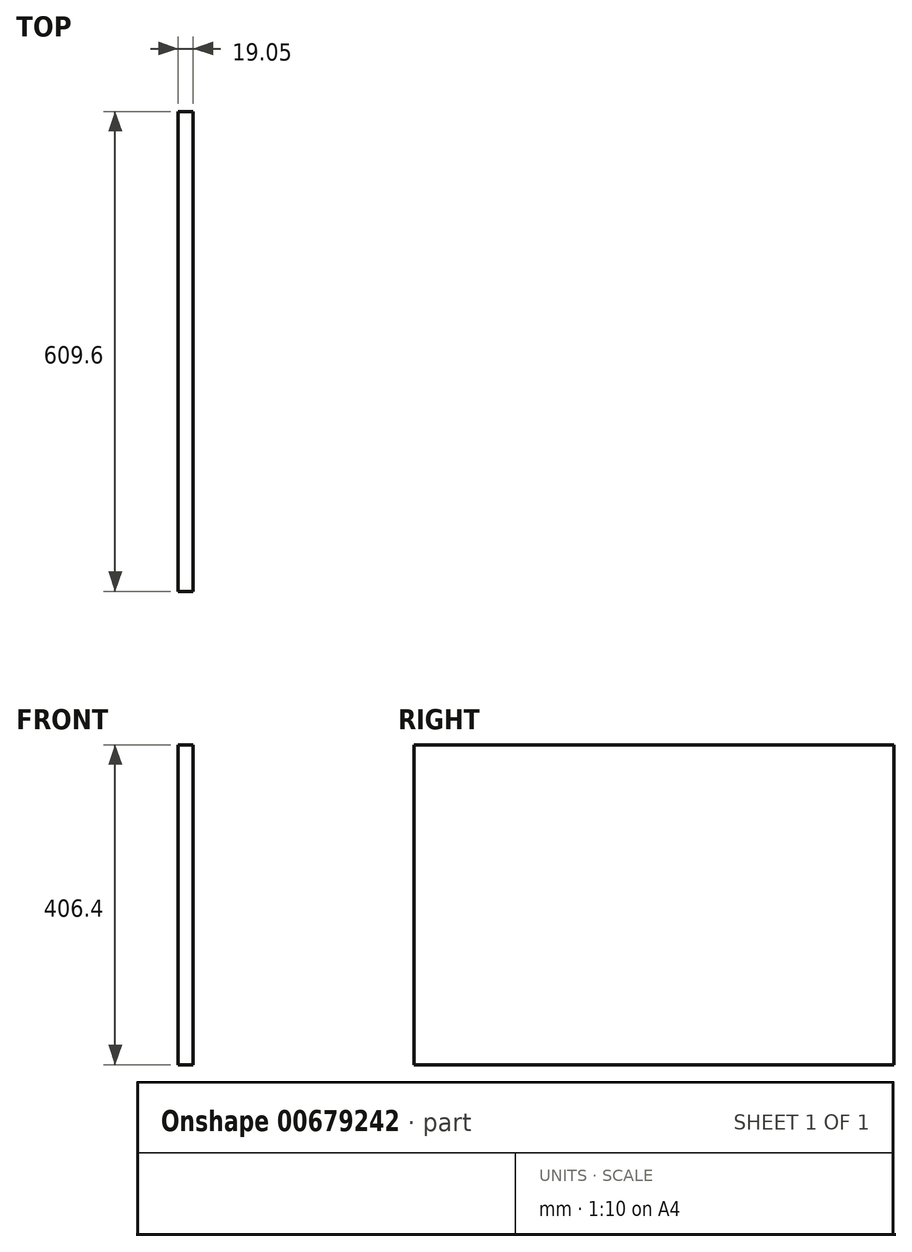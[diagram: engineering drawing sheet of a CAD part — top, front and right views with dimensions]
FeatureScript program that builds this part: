
annotation { "Feature Type Name" : "Feature", "Feature Type Description" : "" }
export const myFeature = defineFeature(function(context is Context, id is Id, definition is map)
    precondition{}
    {
        {
            var Q0;
            Q0=qCreatedBy(makeId("Right.planeOp"),FACE);
            var sketch = newSketch(context, id + "F0", { "sketchPlane" : qUnion([Q0])});
            skLineSegment(sketch, "E0.bottom", {"start": v(304.8, 203.2) * mm, "end": v(-304.8, 203.2) * mm});
            skLineSegment(sketch, "E0.top", {"start": v(304.8, -203.2) * mm, "end": v(-304.8, -203.2) * mm});
            skLineSegment(sketch, "E0.left", {"start": v(304.8, 203.2) * mm, "end": v(304.8, -203.2) * mm});
            skLineSegment(sketch, "E0.right", {"start": v(-304.8, 203.2) * mm, "end": v(-304.8, -203.2) * mm});
            skPoint(sketch, "E0.middle", {"position": v(0, 0) * mm});
            skSolve(sketch);
        }
        {
            var Q0;
            Q0=makeQuery(id+"F0.imprint","IMPRINT",FACE,{"disambiguationData":[TD([[makeQuery(id+"F0.imprint","IMPRINT",EDGE,{"derivedFrom":sQuery(id+"F0.wireOp",EDGE,"E0.bottom")}),1.0]])]});
            extrude(context, id + "F1", {"entities" : qUnion([Q0]), "depth" : 19.05 * mm, "offsetDistance" : 25.4 * mm});
        }
    });
